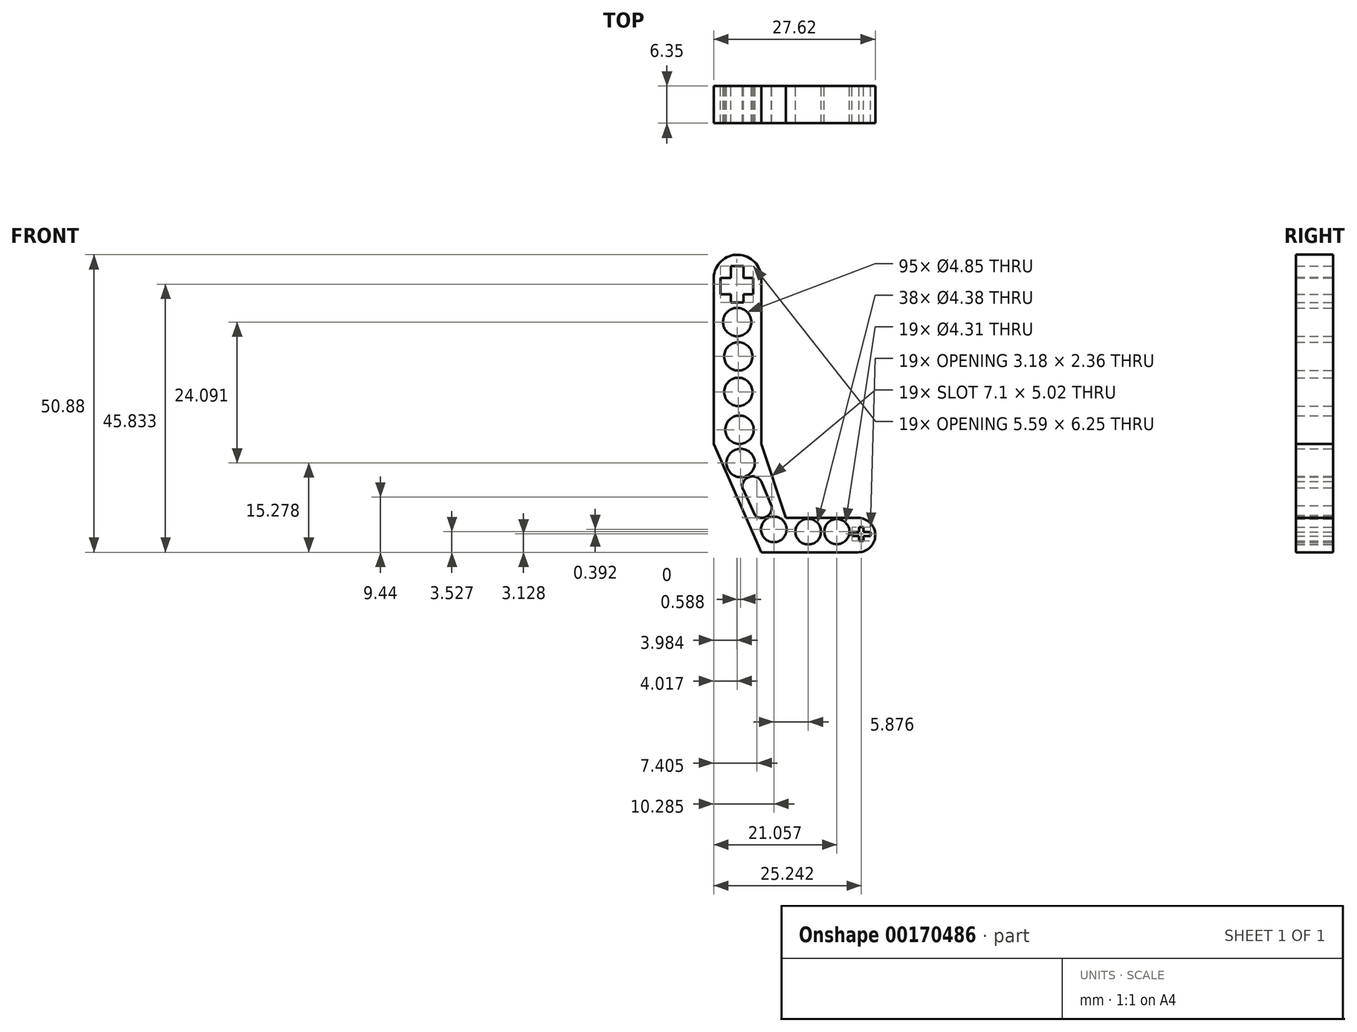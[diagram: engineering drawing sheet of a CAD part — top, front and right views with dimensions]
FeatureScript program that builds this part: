
annotation { "Feature Type Name" : "Feature", "Feature Type Description" : "" }
export const myFeature = defineFeature(function(context is Context, id is Id, definition is map)
    precondition{}
    {
        {
            var Q0;
            Q0=qCreatedBy(makeId("Front.planeOp"),FACE);
            var sketch = newSketch(context, id + "F0", { "sketchPlane" : qUnion([Q0])});
            skLineSegment(sketch, "E0", {"start": v(-8.13, 0) * mm, "end": v(-8.13, 28.5) * mm});
            skLineSegment(sketch, "E1", {"start": v(0, 0) * mm, "end": v(0, 28.3) * mm});
            skArc(sketch, "E2", {"start": v(0, 28.3) * mm, "mid": v(-3.97, 32.37) * mm, "end": v(-8.13, 28.5) * mm});
            skLineSegment(sketch, "E3", {"start": v(-8.13, 0) * mm, "end": v(0, -18.5) * mm});
            skLineSegment(sketch, "E4", {"start": v(0, -18.5) * mm, "end": v(0, 0) * mm});
            skLineSegment(sketch, "E5", {"start": v(0, 0) * mm, "end": v(4.21, -12.63) * mm});
            skLineSegment(sketch, "E6", {"start": v(4.21, -12.63) * mm, "end": v(16.55, -12.63) * mm});
            skLineSegment(sketch, "E7", {"start": v(0, -18.5) * mm, "end": v(16.55, -18.5) * mm});
            skArc(sketch, "E8", {"start": v(16.55, -18.5) * mm, "mid": v(19.49, -15.57) * mm, "end": v(16.55, -12.63) * mm});
            skSolve(sketch);
        }
        {
            var Q0;
            Q0 = qSketchRegion(id + "F0", true);
            extrude(context, id + "F1", {"entities" : qUnion([Q0]), "depth" : 6.35 * mm});
        }
        {
            var Q0;
            Q0=qCreatedBy(makeId("Front.planeOp"),FACE);
            var sketch = newSketch(context, id + "F2", { "sketchPlane" : qUnion([Q0])});
            skLineSegment(sketch, "E9.bottom", {"start": v(-3.01, 24.2) * mm, "end": v(-5.22, 24.2) * mm});
            skLineSegment(sketch, "E9.top", {"start": v(-3.01, 30.45) * mm, "end": v(-5.22, 30.45) * mm});
            skLineSegment(sketch, "E9.left", {"start": v(-3.01, 24.2) * mm, "end": v(-3.01, 30.45) * mm});
            skLineSegment(sketch, "E9.right", {"start": v(-5.22, 24.2) * mm, "end": v(-5.22, 30.45) * mm});
            skPoint(sketch, "E9.middle", {"position": v(-4.12, 27.32) * mm});
            skLineSegment(sketch, "E10", {"start": v(-6.94, 28.4) * mm, "end": v(-1.35, 28.4) * mm});
            skLineSegment(sketch, "E11", {"start": v(-1.35, 28.4) * mm, "end": v(-1.35, 25.63) * mm});
            skLineSegment(sketch, "E12", {"start": v(-1.35, 25.63) * mm, "end": v(-6.94, 25.63) * mm});
            skLineSegment(sketch, "E13", {"start": v(-6.94, 25.63) * mm, "end": v(-6.94, 28.4) * mm});
            skSolve(sketch);
        }
        {
            var Q0;
            Q0 = qSketchRegion(id + "F2", true);
            extrude(context, id + "F3", {"entities" : qUnion([Q0]), "operationType" : NewBodyOperationType.REMOVE, "depth" : 25.4 * mm});
        }
        {
            var Q0;
            Q0=qCreatedBy(makeId("Front.planeOp"),FACE);
            var sketch = newSketch(context, id + "F4", { "sketchPlane" : qUnion([Q0])});
            skCircle(sketch, "E14", {"center": v(-4.11, 20.86) * mm, "radius": 2.42 * mm});
            skCircle(sketch, "E15", {"center": v(-3.92, 14.98) * mm, "radius": 2.42 * mm});
            skCircle(sketch, "E16", {"center": v(-3.92, 8.91) * mm, "radius": 2.42 * mm});
            skCircle(sketch, "E17", {"center": v(-3.72, 2.45) * mm, "radius": 2.42 * mm});
            skCircle(sketch, "E18", {"center": v(-3.53, -3.23) * mm, "radius": 2.42 * mm});
            skCircle(sketch, "E19", {"center": v(2.15, -14.6) * mm, "radius": 2.19 * mm});
            skCircle(sketch, "E20", {"center": v(8.03, -14.98) * mm, "radius": 2.19 * mm});
            skCircle(sketch, "E21", {"center": v(12.93, -14.98) * mm, "radius": 2.15 * mm});
            skSolve(sketch);
        }
        {
            var Q0;
            Q0 = qSketchRegion(id + "F4", true);
            extrude(context, id + "F5", {"entities" : qUnion([Q0]), "operationType" : NewBodyOperationType.REMOVE, "depth" : 25.4 * mm});
        }
        {
            var Q0;
            Q0=qCreatedBy(makeId("Front.planeOp"),FACE);
            var sketch = newSketch(context, id + "F6", { "sketchPlane" : qUnion([Q0])});
            skLineSegment(sketch, "E22", {"start": v(-3.24, -7.5) * mm, "end": v(-1.06, -12.2) * mm});
            skLineSegment(sketch, "E23", {"start": v(0, -6.37) * mm, "end": v(1.75, -10.5) * mm});
            skArc(sketch, "E24", {"start": v(-1.06, -12.2) * mm, "mid": v(0.96, -12.38) * mm, "end": v(1.75, -10.5) * mm});
            skArc(sketch, "E25", {"start": v(0, -6.37) * mm, "mid": v(-2.08, -5.62) * mm, "end": v(-3.24, -7.5) * mm});
            skSolve(sketch);
        }
        {
            var Q0;
            Q0 = qSketchRegion(id + "F6", true);
            extrude(context, id + "F7", {"entities" : qUnion([Q0]), "operationType" : NewBodyOperationType.REMOVE, "depth" : 25.4 * mm});
        }
        {
            var Q0;
            Q0=qCreatedBy(makeId("Front.planeOp"),FACE);
            var sketch = newSketch(context, id + "F8", { "sketchPlane" : qUnion([Q0])});
            skLineSegment(sketch, "E26.bottom", {"start": v(17.5, -16.56) * mm, "end": v(16.73, -16.56) * mm});
            skLineSegment(sketch, "E26.top", {"start": v(17.5, -14.2) * mm, "end": v(16.73, -14.2) * mm});
            skLineSegment(sketch, "E26.left", {"start": v(17.5, -16.56) * mm, "end": v(17.5, -14.2) * mm});
            skLineSegment(sketch, "E26.right", {"start": v(16.73, -16.56) * mm, "end": v(16.73, -14.2) * mm});
            skPoint(sketch, "E26.middle", {"position": v(17.11, -15.38) * mm});
            skLineSegment(sketch, "E27.bottom", {"start": v(18.7, -15.73) * mm, "end": v(15.52, -15.73) * mm});
            skLineSegment(sketch, "E27.top", {"start": v(18.7, -15.04) * mm, "end": v(15.52, -15.04) * mm});
            skLineSegment(sketch, "E27.left", {"start": v(18.7, -15.73) * mm, "end": v(18.7, -15.04) * mm});
            skLineSegment(sketch, "E27.right", {"start": v(15.52, -15.73) * mm, "end": v(15.52, -15.04) * mm});
            skSolve(sketch);
        }
        {
            var Q0;
            Q0 = qSketchRegion(id + "F8", true);
            extrude(context, id + "F9", {"entities" : qUnion([Q0]), "operationType" : NewBodyOperationType.REMOVE, "depth" : 25.4 * mm});
        }
    });
